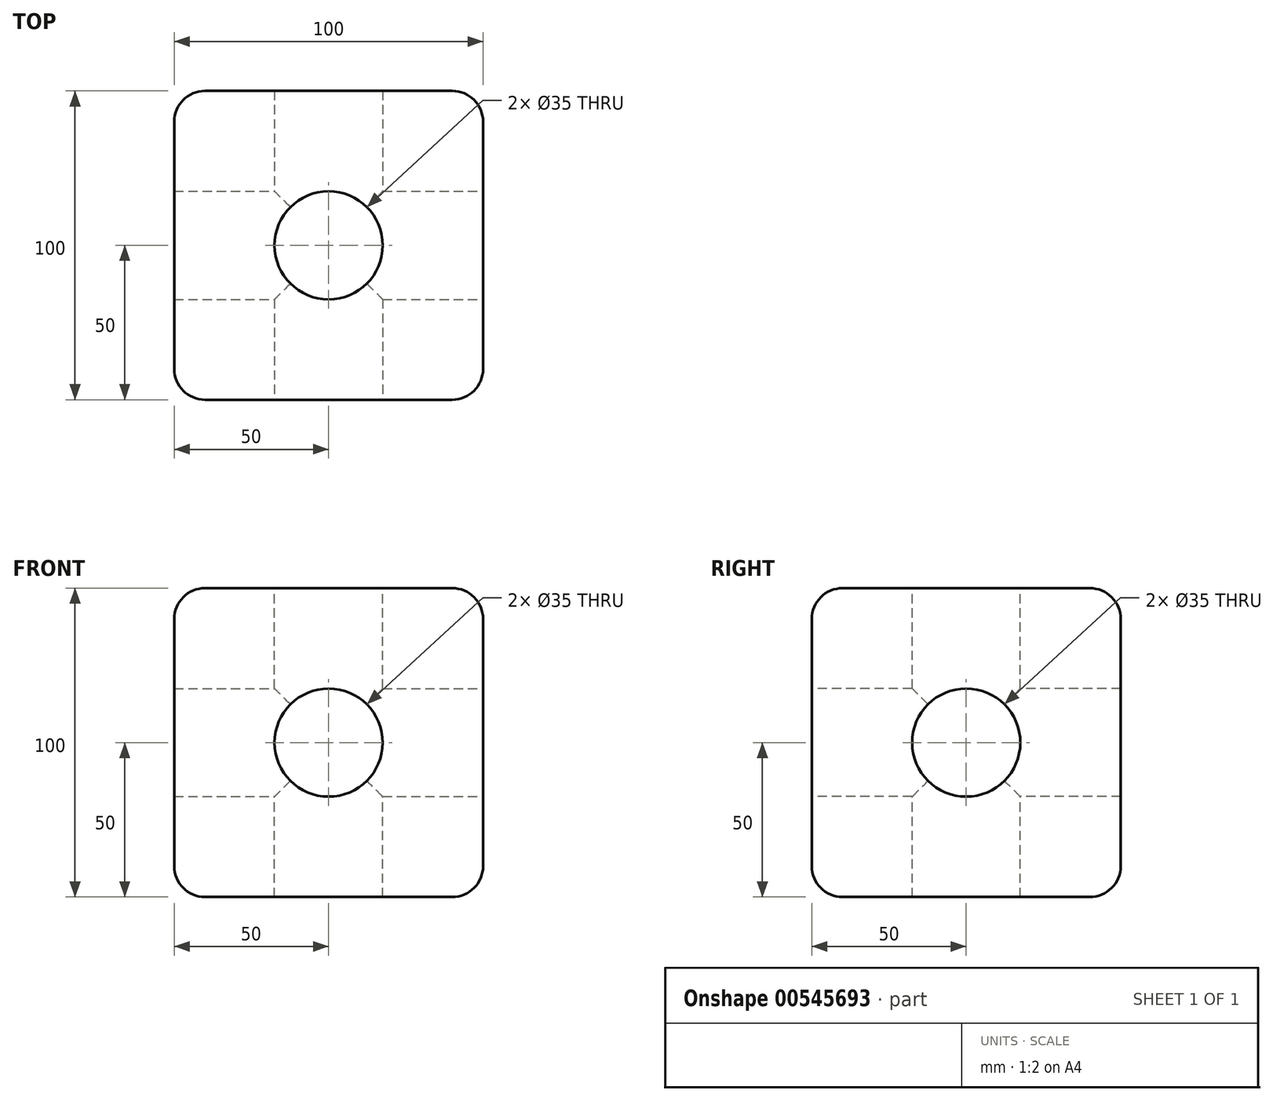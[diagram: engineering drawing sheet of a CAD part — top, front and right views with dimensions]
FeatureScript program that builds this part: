
annotation { "Feature Type Name" : "Feature", "Feature Type Description" : "" }
export const myFeature = defineFeature(function(context is Context, id is Id, definition is map)
    precondition{}
    {
        {
            var Q0;
            Q0=qCreatedBy(makeId("Front.planeOp"),FACE);
            var sketch = newSketch(context, id + "F0", { "sketchPlane" : qUnion([Q0])});
            skLineSegment(sketch, "E0.bottom", {"start": v(50, -50) * mm, "end": v(-50, -50) * mm});
            skLineSegment(sketch, "E0.top", {"start": v(50, 50) * mm, "end": v(-50, 50) * mm});
            skLineSegment(sketch, "E0.left", {"start": v(50, -50) * mm, "end": v(50, 50) * mm});
            skLineSegment(sketch, "E0.right", {"start": v(-50, -50) * mm, "end": v(-50, 50) * mm});
            skPoint(sketch, "E0.middle", {"position": v(0, 0) * mm});
            skSolve(sketch);
        }
        {
            var Q0;
            Q0=makeQuery(id+"F0.imprint","IMPRINT",FACE,{"disambiguationData":[TD([[makeQuery(id+"F0.imprint","IMPRINT",EDGE,{"derivedFrom":sQuery(id+"F0.wireOp",EDGE,"E0.bottom")}),-1.0]])]});
            extrude(context, id + "F1", {"entities" : qUnion([Q0]), "endBound" : BoundingType.SYMMETRIC, "depth" : 100 * mm, "offsetDistance" : 25 * mm});
        }
        {
            var Q0;
            Q0=makeQuery(id+"F1.opExtrude","CAP_FACE",FACE,{"disambiguationData":[OSD([sQuery(id+"F0.wireOp",EDGE,"E0.bottom"),sQuery(id+"F0.wireOp",EDGE,"E0.top"),sQuery(id+"F0.wireOp",EDGE,"E0.left"),sQuery(id+"F0.wireOp",EDGE,"E0.right")])],"isStart":false});
            var sketch = newSketch(context, id + "F2", { "sketchPlane" : qUnion([Q0])});
            skCircle(sketch, "E1", {"center": v(0, 0) * mm, "radius": 17.5 * mm});
            skSolve(sketch);
        }
        {
            var Q0;
            Q0 = qSketchRegion(id + "F2", true);
            var Q1;
            Q1=makeQuery(id+"F1.opExtrude","CAP_FACE",FACE,{"disambiguationData":[OSD([sQuery(id+"F0.wireOp",EDGE,"E0.bottom"),sQuery(id+"F0.wireOp",EDGE,"E0.top"),sQuery(id+"F0.wireOp",EDGE,"E0.left"),sQuery(id+"F0.wireOp",EDGE,"E0.right")])],"isStart":true});
            extrude(context, id + "F3", {"entities" : qUnion([Q0]), "operationType" : NewBodyOperationType.REMOVE, "endBound" : BoundingType.UP_TO_SURFACE, "oppositeDirection" : true, "depth" : 25 * mm, "endBoundEntityFace" : qUnion([Q1]), "offsetDistance" : 25 * mm});
        }
        {
            var Q0;
            Q0=makeQuery(id+"F1.opExtrude","SWEPT_FACE",FACE,{"disambiguationData":[OSD([sQuery(id+"F0.wireOp",EDGE,"E0.left")])]});
            var sketch = newSketch(context, id + "F4", { "sketchPlane" : qUnion([Q0])});
            skCircle(sketch, "E2", {"center": v(0, 0) * mm, "radius": 17.5 * mm});
            skSolve(sketch);
        }
        {
            var Q0;
            Q0 = qSketchRegion(id + "F4", true);
            var Q1;
            Q1=makeQuery(id+"F1.opExtrude","SWEPT_FACE",FACE,{"disambiguationData":[OSD([sQuery(id+"F0.wireOp",EDGE,"E0.right")])]});
            extrude(context, id + "F5", {"entities" : qUnion([Q0]), "operationType" : NewBodyOperationType.REMOVE, "endBound" : BoundingType.UP_TO_SURFACE, "oppositeDirection" : true, "depth" : 25 * mm, "endBoundEntityFace" : qUnion([Q1]), "offsetDistance" : 25 * mm});
        }
        {
            var Q0;
            Q0=makeQuery(id+"F1.opExtrude","SWEPT_FACE",FACE,{"disambiguationData":[OSD([sQuery(id+"F0.wireOp",EDGE,"E0.top")])]});
            var sketch = newSketch(context, id + "F6", { "sketchPlane" : qUnion([Q0])});
            skCircle(sketch, "E3", {"center": v(0, 0) * mm, "radius": 17.5 * mm});
            skSolve(sketch);
        }
        {
            var Q0;
            Q0 = qSketchRegion(id + "F6", true);
            var Q1;
            Q1=makeQuery(id+"F1.opExtrude","SWEPT_FACE",FACE,{"disambiguationData":[OSD([sQuery(id+"F0.wireOp",EDGE,"E0.bottom")])]});
            extrude(context, id + "F7", {"entities" : qUnion([Q0]), "operationType" : NewBodyOperationType.REMOVE, "endBound" : BoundingType.UP_TO_SURFACE, "oppositeDirection" : true, "depth" : 25 * mm, "endBoundEntityFace" : qUnion([Q1]), "offsetDistance" : 25 * mm});
        }
        {
            var Q0;
            Q0=makeQuery(id+"F1.opExtrude","SWEPT_EDGE",EDGE,{"disambiguationData":[OSD([sQuery(id+"F0.wireOp",EDGE,"E0.top"),sQuery(id+"F0.wireOp",EDGE,"E0.left")])]});
            var Q1;
            Q1=makeQuery(id+"F1.opExtrude","CAP_EDGE",EDGE,{"disambiguationData":[OSD([sQuery(id+"F0.wireOp",EDGE,"E0.left")])],"isStart":true});
            var Q2;
            Q2=makeQuery(id+"F1.opExtrude","SWEPT_EDGE",EDGE,{"disambiguationData":[OSD([sQuery(id+"F0.wireOp",EDGE,"E0.bottom"),sQuery(id+"F0.wireOp",EDGE,"E0.left")])]});
            var Q3;
            Q3=makeQuery(id+"F1.opExtrude","CAP_EDGE",EDGE,{"disambiguationData":[OSD([sQuery(id+"F0.wireOp",EDGE,"E0.left")])],"isStart":false});
            var Q4;
            Q4=makeQuery(id+"F1.opExtrude","CAP_EDGE",EDGE,{"disambiguationData":[OSD([sQuery(id+"F0.wireOp",EDGE,"E0.top")])],"isStart":false});
            var Q5;
            Q5=makeQuery(id+"F1.opExtrude","SWEPT_EDGE",EDGE,{"disambiguationData":[OSD([sQuery(id+"F0.wireOp",EDGE,"E0.top"),sQuery(id+"F0.wireOp",EDGE,"E0.right")])]});
            var Q6;
            Q6=makeQuery(id+"F1.opExtrude","CAP_EDGE",EDGE,{"disambiguationData":[OSD([sQuery(id+"F0.wireOp",EDGE,"E0.top")])],"isStart":true});
            var Q7;
            Q7=makeQuery(id+"F1.opExtrude","CAP_EDGE",EDGE,{"disambiguationData":[OSD([sQuery(id+"F0.wireOp",EDGE,"E0.right")])],"isStart":true});
            var Q8;
            Q8=makeQuery(id+"F1.opExtrude","CAP_EDGE",EDGE,{"disambiguationData":[OSD([sQuery(id+"F0.wireOp",EDGE,"E0.bottom")])],"isStart":true});
            var Q9;
            Q9=makeQuery(id+"F1.opExtrude","SWEPT_EDGE",EDGE,{"disambiguationData":[OSD([sQuery(id+"F0.wireOp",EDGE,"E0.bottom"),sQuery(id+"F0.wireOp",EDGE,"E0.right")])]});
            var Q10;
            Q10=makeQuery(id+"F1.opExtrude","CAP_EDGE",EDGE,{"disambiguationData":[OSD([sQuery(id+"F0.wireOp",EDGE,"E0.right")])],"isStart":false});
            var Q11;
            Q11=makeQuery(id+"F1.opExtrude","CAP_EDGE",EDGE,{"disambiguationData":[OSD([sQuery(id+"F0.wireOp",EDGE,"E0.bottom")])],"isStart":false});
            fillet(context, id + "F8", {"entities" : qUnion([Q0, Q1, Q2, Q3, Q4, Q5, Q6, Q7, Q8, Q9, Q10, Q11]), "radius" : 10 * mm, "tangentPropagation" : true, "allowEdgeOverflow" : false});
        }
    });
